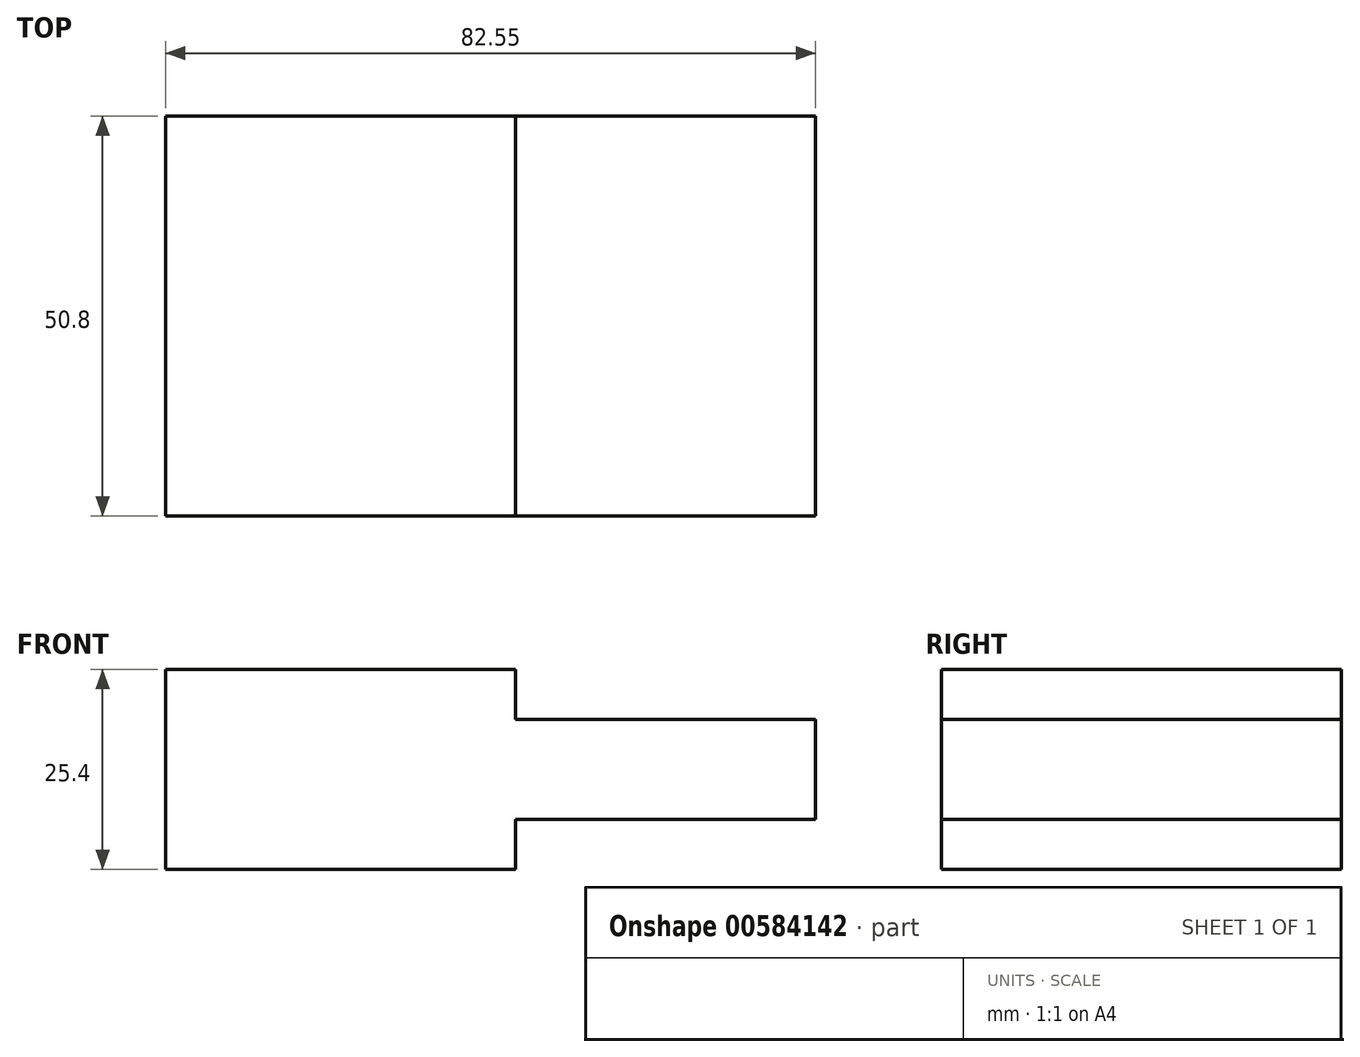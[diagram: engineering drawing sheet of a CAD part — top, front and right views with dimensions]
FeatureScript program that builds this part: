
annotation { "Feature Type Name" : "Feature", "Feature Type Description" : "" }
export const myFeature = defineFeature(function(context is Context, id is Id, definition is map)
    precondition{}
    {
        {
            var Q0;
            Q0=qCreatedBy(makeId("Front.planeOp"),FACE);
            var sketch = newSketch(context, id + "F0", { "sketchPlane" : qUnion([Q0])});
            skLineSegment(sketch, "E0", {"start": v(0, 0) * mm, "end": v(44.45, 0) * mm});
            skLineSegment(sketch, "E1", {"start": v(44.45, 0) * mm, "end": v(44.45, 6.35) * mm});
            skLineSegment(sketch, "E2", {"start": v(44.45, 6.35) * mm, "end": v(82.55, 6.35) * mm});
            skLineSegment(sketch, "E3", {"start": v(82.55, 6.35) * mm, "end": v(82.55, 19.05) * mm});
            skLineSegment(sketch, "E4", {"start": v(82.55, 19.05) * mm, "end": v(44.45, 19.05) * mm});
            skLineSegment(sketch, "E5", {"start": v(44.45, 19.05) * mm, "end": v(44.45, 25.4) * mm});
            skLineSegment(sketch, "E6", {"start": v(44.45, 25.4) * mm, "end": v(0, 25.4) * mm});
            skLineSegment(sketch, "E7", {"start": v(0, 25.4) * mm, "end": v(0, 0) * mm});
            skSolve(sketch);
        }
        {
            var Q0;
            Q0=makeQuery(id+"F0.imprint","IMPRINT",FACE,{"disambiguationData":[TD([[makeQuery(id+"F0.imprint","IMPRINT",EDGE,{"derivedFrom":sQuery(id+"F0.wireOp",EDGE,"E0")}),1.0]])]});
            extrude(context, id + "F1", {"entities" : qUnion([Q0]), "depth" : 50.8 * mm, "offsetDistance" : 25.4 * mm});
        }
    });
